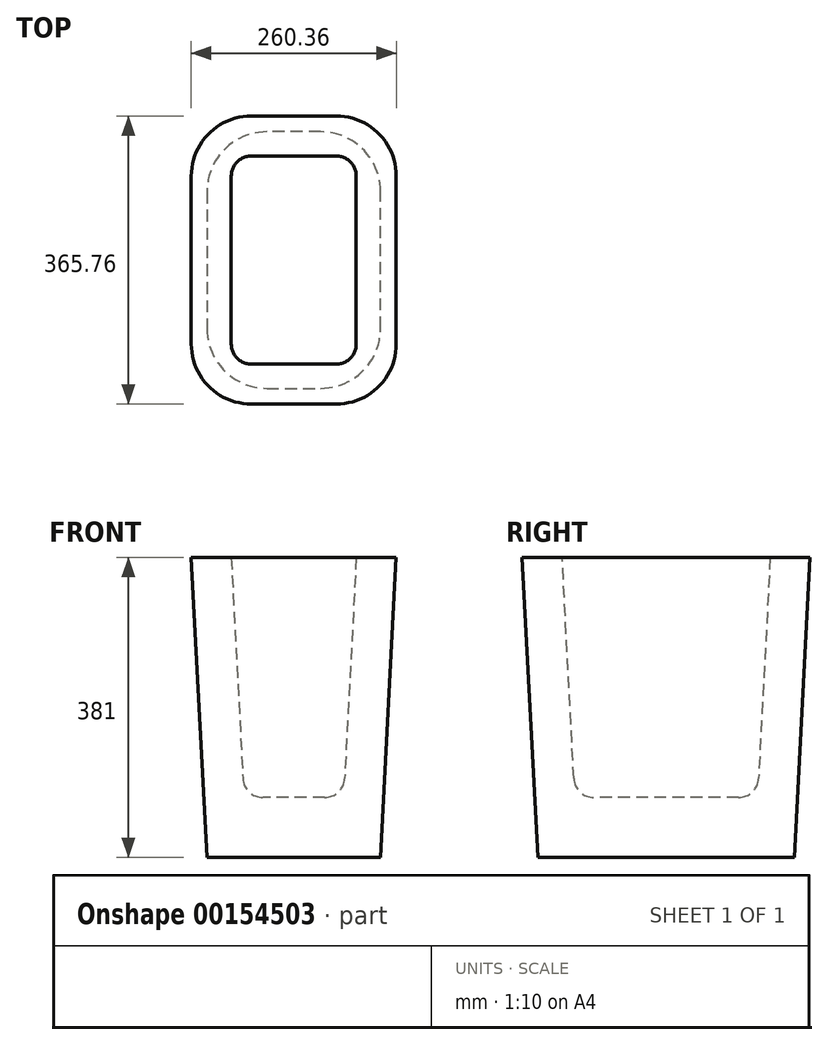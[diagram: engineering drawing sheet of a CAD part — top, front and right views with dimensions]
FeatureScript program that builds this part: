
annotation { "Feature Type Name" : "Feature", "Feature Type Description" : "" }
export const myFeature = defineFeature(function(context is Context, id is Id, definition is map)
    precondition{}
    {
        {
            var Q0;
            Q0=qCreatedBy(makeId("Top.planeOp"),FACE);
            var sketch = newSketch(context, id + "F0", { "sketchPlane" : qUnion([Q0])});
            skLineSegment(sketch, "E0.bottom", {"start": v(130.17, 182.88) * mm, "end": v(-130.18, 182.88) * mm});
            skLineSegment(sketch, "E0.top", {"start": v(130.18, -182.88) * mm, "end": v(-130.17, -182.88) * mm});
            skLineSegment(sketch, "E0.left", {"start": v(130.18, 182.88) * mm, "end": v(130.18, -182.88) * mm});
            skLineSegment(sketch, "E0.right", {"start": v(-130.18, 182.88) * mm, "end": v(-130.17, -182.88) * mm});
            skPoint(sketch, "E0.middle", {"position": v(0, 0) * mm});
            skLineSegment(sketch, "E1.0", {"start": v(79.38, 132.08) * mm, "end": v(-79.38, 132.08) * mm});
            skLineSegment(sketch, "E1.1", {"start": v(79.38, 132.08) * mm, "end": v(79.38, -132.08) * mm});
            skLineSegment(sketch, "E1.2", {"start": v(79.38, -132.08) * mm, "end": v(-79.37, -132.08) * mm});
            skLineSegment(sketch, "E1.3", {"start": v(-79.38, 132.08) * mm, "end": v(-79.37, -132.08) * mm});
            skSolve(sketch);
        }
        {
            var Q0;
            Q0=makeQuery(id+"F0.imprint","IMPRINT",FACE,{"disambiguationData":[TD([[makeQuery(id+"F0.imprint","IMPRINT",EDGE,{"derivedFrom":sQuery(id+"F0.wireOp",EDGE,"E0.bottom")}),1.0]])]});
            var Q1;
            Q1=makeQuery(id+"F0.imprint","IMPRINT",FACE,{"disambiguationData":[TD([[makeQuery(id+"F0.imprint","IMPRINT",EDGE,{"derivedFrom":sQuery(id+"F0.wireOp",EDGE,"E1.0")}),1.0]])]});
            extrude(context, id + "F1", {"entities" : qUnion([Q0, Q1]), "oppositeDirection" : true, "depth" : 381 * mm, "hasDraft" : true, "draftAngle" : 3 * degree, "draftPullDirection" : true});
        }
        {
            var Q0;
            Q0=makeQuery(id+"F1.opExtrude","SWEPT_EDGE",EDGE,{"disambiguationData":[OSD([sQuery(id+"F0.wireOp",EDGE,"E0.top"),sQuery(id+"F0.wireOp",EDGE,"E0.right")])]});
            var Q1;
            Q1=makeQuery(id+"F1.opExtrude","SWEPT_EDGE",EDGE,{"disambiguationData":[OSD([sQuery(id+"F0.wireOp",EDGE,"E0.top"),sQuery(id+"F0.wireOp",EDGE,"E0.left")])]});
            var Q2;
            Q2=makeQuery(id+"F1.opExtrude","SWEPT_EDGE",EDGE,{"disambiguationData":[OSD([sQuery(id+"F0.wireOp",EDGE,"E0.bottom"),sQuery(id+"F0.wireOp",EDGE,"E0.left")])]});
            var Q3;
            Q3=makeQuery(id+"F1.opExtrude","SWEPT_EDGE",EDGE,{"disambiguationData":[OSD([sQuery(id+"F0.wireOp",EDGE,"E0.bottom"),sQuery(id+"F0.wireOp",EDGE,"E0.right")])]});
            fillet(context, id + "F2", {"entities" : qUnion([Q0, Q1, Q2, Q3]), "radius" : 76.2 * mm, "tangentPropagation" : true, "allowEdgeOverflow" : false});
        }
        {
            var Q0;
            Q0=makeQuery(id+"F0.imprint","IMPRINT",FACE,{"disambiguationData":[TD([[makeQuery(id+"F0.imprint","IMPRINT",EDGE,{"derivedFrom":sQuery(id+"F0.wireOp",EDGE,"E1.0")}),1.0]])]});
            extrude(context, id + "F3", {"entities" : qUnion([Q0]), "operationType" : NewBodyOperationType.REMOVE, "oppositeDirection" : true, "depth" : 304.8 * mm, "hasDraft" : true, "draftAngle" : 3 * degree, "draftPullDirection" : true});
        }
        {
            var Q0;
            Q0=makeQuery(id+"F3.boolean.opBoolean","COPY",FACE,{"derivedFrom":makeQuery(id+"F3.opExtrude","CAP_FACE",FACE,{"disambiguationData":[OSD([sQuery(id+"F0.wireOp",EDGE,"E1.0"),sQuery(id+"F0.wireOp",EDGE,"E1.1"),sQuery(id+"F0.wireOp",EDGE,"E1.2"),sQuery(id+"F0.wireOp",EDGE,"E1.3")])],"isStart":false})});
            var Q1;
            Q1=makeQuery(id+"F3.boolean.opBoolean","COPY",EDGE,{"derivedFrom":makeQuery(id+"F3.opExtrude","SWEPT_EDGE",EDGE,{"disambiguationData":[OSD([sQuery(id+"F0.wireOp",EDGE,"E1.0"),sQuery(id+"F0.wireOp",EDGE,"E1.3")])]})});
            var Q2;
            Q2=makeQuery(id+"F3.boolean.opBoolean","COPY",EDGE,{"derivedFrom":makeQuery(id+"F3.opExtrude","SWEPT_EDGE",EDGE,{"disambiguationData":[OSD([sQuery(id+"F0.wireOp",EDGE,"E1.0"),sQuery(id+"F0.wireOp",EDGE,"E1.1")])]})});
            var Q3;
            Q3=makeQuery(id+"F3.boolean.opBoolean","COPY",EDGE,{"derivedFrom":makeQuery(id+"F3.opExtrude","SWEPT_EDGE",EDGE,{"disambiguationData":[OSD([sQuery(id+"F0.wireOp",EDGE,"E1.1"),sQuery(id+"F0.wireOp",EDGE,"E1.2")])]})});
            var Q4;
            Q4=makeQuery(id+"F3.boolean.opBoolean","COPY",EDGE,{"derivedFrom":makeQuery(id+"F3.opExtrude","SWEPT_EDGE",EDGE,{"disambiguationData":[OSD([sQuery(id+"F0.wireOp",EDGE,"E1.2"),sQuery(id+"F0.wireOp",EDGE,"E1.3")])]})});
            fillet(context, id + "F4", {"entities" : qUnion([Q0, Q1, Q2, Q3, Q4]), "radius" : 25.4 * mm, "tangentPropagation" : true, "allowEdgeOverflow" : false});
        }
    });
